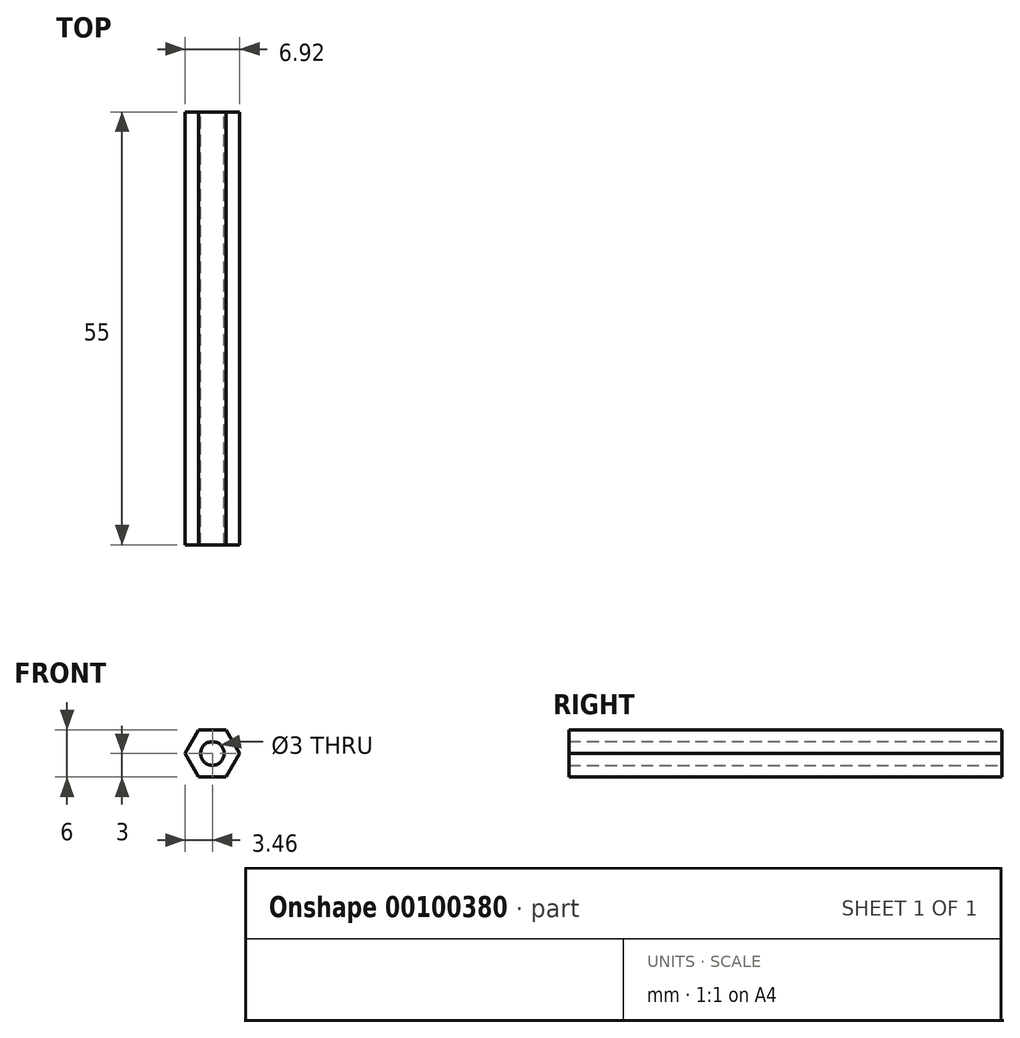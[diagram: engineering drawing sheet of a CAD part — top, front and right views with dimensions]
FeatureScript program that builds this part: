
annotation { "Feature Type Name" : "Feature", "Feature Type Description" : "" }
export const myFeature = defineFeature(function(context is Context, id is Id, definition is map)
    precondition{}
    {
        {
            var Q0;
            Q0=qCreatedBy(makeId("Front.planeOp"),FACE);
            var sketch = newSketch(context, id + "F0", { "sketchPlane" : qUnion([Q0])});
            skCircle(sketch, "E0.cCircle", {"center": v(0, 3) * mm, "radius": 3 * mm, "construction": true});
            skLineSegment(sketch, "E0.0", {"start": v(1.73, 6) * mm, "end": v(3.46, 3) * mm});
            skLineSegment(sketch, "E0.1", {"start": v(3.46, 3) * mm, "end": v(1.73, 0) * mm});
            skLineSegment(sketch, "E0.2", {"start": v(1.73, 0) * mm, "end": v(-1.73, 0) * mm});
            skLineSegment(sketch, "E0.3", {"start": v(-1.73, 0) * mm, "end": v(-3.46, 3) * mm});
            skLineSegment(sketch, "E0.4", {"start": v(-3.46, 3) * mm, "end": v(-1.73, 6) * mm});
            skLineSegment(sketch, "E0.5", {"start": v(-1.73, 6) * mm, "end": v(1.73, 6) * mm});
            skPoint(sketch, "E0.0.midPoint", {"position": v(2.6, 4.5) * mm});
            skPoint(sketch, "E1", {"position": v(0, 0) * mm});
            skCircle(sketch, "E2", {"center": v(0, 3) * mm, "radius": 1.5 * mm});
            skSolve(sketch);
        }
        {
            assignVariable(context, id + "F1", {"name" : "BoltShaftLength", "anyValue" : 25});
        }
        {
            assignVariable(context, id + "F2", {"name" : "StandoffLength", "anyValue" : (2 * getVariable(context, 'BoltShaftLength')) + 5});
        }
        {
            var Q0;
            Q0=makeQuery(id+"F0.imprint","IMPRINT",FACE,{"disambiguationData":[TD([[makeQuery(id+"F0.imprint","IMPRINT",EDGE,{"derivedFrom":sQuery(id+"F0.wireOp",EDGE,"E0.0")}),-1.0]])]});
            extrude(context, id + "F3", {"entities" : qUnion([Q0]), "endBound" : BoundingType.SYMMETRIC, "depth" : (getVariable(context, 'StandoffLength')) * mm});
        }
    });
